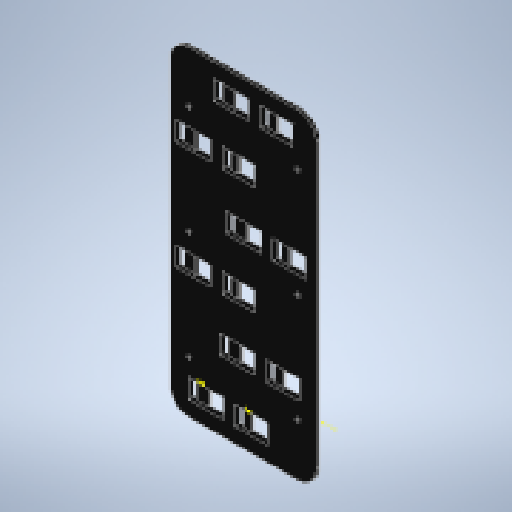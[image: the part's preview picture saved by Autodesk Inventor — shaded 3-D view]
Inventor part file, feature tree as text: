
AUTODESK INVENTOR PART (.ipt)
format: ipt  version: 2024.1 (Build 281209000, 209)  size: 614,912 bytes
history: native  units: mm
features: reference x29, projected_geometry x9, sketch x8, extrude x7, other x4, chamfer x4, plane x2, fillet x1
ambient origin geometry x8: Origin, YZ Plane, XZ Plane, XY Plane, X Axis, Y Axis, Z Axis, Center Point
bodies: Solid2 (feature_tree)
feature tree (64):
  other  "back-plate"
  plane  "Work Plane1"
  extrude  "Extrusion12"  Depth=19.0mm
  extrude  "Extrusion13"  Depth=47.0mm
  extrude  "Extrusion14"  Depth=19.2mm
  sketch  "Sketch14"  dims[d81=43.0mm]
  plane  "Work Plane2"
  chamfer  "Chamfer10"  Distance=1.5mm
  extrude  "Extrusion15"  Depth=15.0mm
  chamfer  "Chamfer11"  Distance=254.0mm
  extrude  "Extrusion5"  Depth=5.0mm TaperAngle=45.0deg
  sketch  "Sketch Driven Pattern1"  dims[d48=0.5mm d49=0.0mm d55=19.0mm d58=19.2mm]
  extrude  "Extrusion6"  Depth=10.0mm
  fillet  "Fillet2"  [1 undecoded]
  chamfer  "Chamfer7"  Distance=3.0mm Angle=45.0deg
  extrude  "Extrusion7"  Depth=10.0mm
  chamfer  "Chamfer8"  Distance=4.0mm
  sketch  "Sketch7"  dims[d60=47.0mm d64=19.0mm]
  sketch  "Sketch8"  dims[d66=19.2mm d68=19.0mm d72=19.2mm d74=19.2mm d78=19.0mm d80=19.0mm]
  reference  "Reference23"
  reference  "Reference24"
  reference  "Reference25"
  reference  "Reference26"
  reference  "Reference27"
  reference  "Reference28"
  reference  "Reference29"
  reference  "Reference30"
  reference  "Reference31"
  reference  "Reference32"
  reference  "Reference33"
  reference  "Reference34"
  reference  "Reference35"
  reference  "Reference36"
  reference  "Reference37"
  reference  "Reference38"
  reference  "Reference39"
  reference  "Reference40"
  reference  "Reference41"
  sketch  "Sketch15"  dims[d82=43.0mm]
  reference  "Reference42"
  reference  "Reference43"
  reference  "Reference44"
  reference  "Reference46"
  reference  "Reference48"
  reference  "Reference52"
  reference  "Reference53"
  reference  "Reference56"
  reference  "Reference57"
  reference  "Reference59"
  sketch  "Sketch16"  dims[d83=43.0mm]
  sketch  "Sketch17"  dims[d84=43.0mm]
  projected_geometry  "Projected Loop12"
  sketch  "Sketch18"  dims[d88=43.0mm d90=1.5mm d91=0.0mm d92=15.0mm d97=254.0mm d98=5.0mm d99=2.0mm d100=45.0deg d101=3.1mm d112=0.0mm d113=0.0mm d114=3.0mm d115=2.0mm d116=45.0deg d143=14.400658mm d147=4.0mm d149=3.7mm d151=4.0mm d152=4.0mm d154=11.0mm d155=11.0mm d156=15.2mm d157=0.0mm d158=2.0mm d159=0.0mm d160=2.0mm d161=0.0mm d162=3.7mm d163=7.107566mm d164=1.0mm d165=2.0mm d166=45.0deg d167=4.0mm d168=2.0mm d169=15.2mm d170=0.0mm d171=2.0mm d172=2.0mm d173=45.0deg d174=4.0mm d175=0.5mm d176=4.199342mm d177=4.199342mm d178=0.1mm d179=0.1mm d180=19.2mm d181=74.892434mm d182=42.8mm d183=74.892434mm d184=74.892434mm d185=25.0mm d186=10.0mm d187=74.892434mm d188=74.892434mm d189=74.892434mm d190=19.2mm d193=116.0mm d194=0.5mm d197=30.0mm d198=15.0mm d199=14.0mm d200=15.0mm d201=14.0mm d203=14.0mm d204=41.2mm d205=41.0mm d206=127.0mm d207=127.0mm d208=10.0mm d209=10.0mm]
  projected_geometry  "Projected Loop13"
  projected_geometry  "Projected Loop14"
  projected_geometry  "Projected Loop18"
  projected_geometry  "Projected Loop21"
  projected_geometry  "Projected Loop22"
  projected_geometry  "Projected Loop23"
  projected_geometry  "Projected Loop24"
  projected_geometry  "Projected Loop25"
  other  "<userpath>\Documents\0004-CAD\3D-cad-main\cable-hanger\VERSION3-largel-upright-hook.iam"
  other  "VERSION3-largel-upright-hook.iam"
  other  "cable-hanger-dual-large:1"
note: 1 required parameter value undecoded (feature->parameter linkage not recoverable at this tier; creation-order binding heuristic only, values carry confidence <= 0.55)
